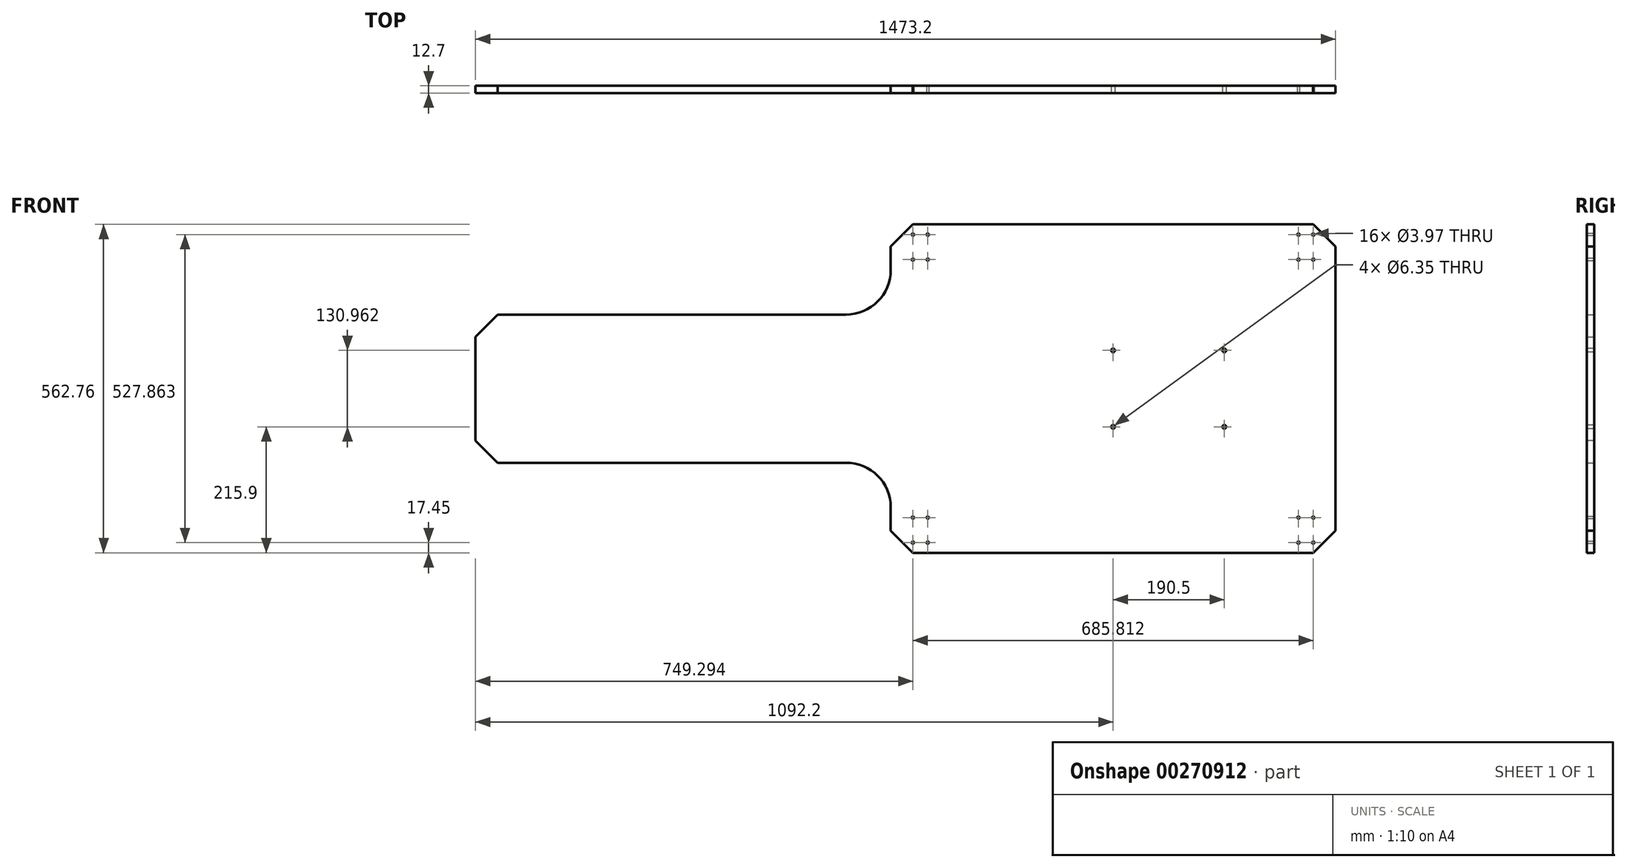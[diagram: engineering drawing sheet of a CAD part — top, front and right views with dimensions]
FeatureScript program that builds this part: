
annotation { "Feature Type Name" : "Feature", "Feature Type Description" : "" }
export const myFeature = defineFeature(function(context is Context, id is Id, definition is map)
    precondition{}
    {
        {
            var Q0;
            Q0=qCreatedBy(makeId("Front.planeOp"),FACE);
            var sketch = newSketch(context, id + "F0", { "sketchPlane" : qUnion([Q0])});
            skLineSegment(sketch, "E0", {"start": v(711.2, 0) * mm, "end": v(1473.2, 0) * mm});
            skLineSegment(sketch, "E1.0", {"start": v(711.2, 562.76) * mm, "end": v(1473.2, 562.76) * mm});
            skLineSegment(sketch, "E2", {"start": v(1473.2, 562.76) * mm, "end": v(1473.2, 0) * mm});
            skLineSegment(sketch, "E3.0", {"start": v(711.2, 0) * mm, "end": v(711.2, 78.18) * mm});
            skLineSegment(sketch, "E4.0", {"start": v(635, 408.38) * mm, "end": v(0, 408.38) * mm});
            skLineSegment(sketch, "E5.MirrorCS", {"start": v(635, 154.38) * mm, "end": v(0, 154.38) * mm});
            skLineSegment(sketch, "E6.trimOffspring", {"start": v(711.2, 484.58) * mm, "end": v(711.2, 562.76) * mm});
            skArc(sketch, "E7.filletArc", {"start": v(635, 408.38) * mm, "mid": v(688.88, 430.7) * mm, "end": v(711.2, 484.58) * mm});
            skArc(sketch, "E8.filletArc", {"start": v(711.2, 78.18) * mm, "mid": v(688.88, 132.06) * mm, "end": v(635, 154.38) * mm});
            skLineSegment(sketch, "E9", {"start": v(0, 408.38) * mm, "end": v(0, 154.38) * mm});
            skSolve(sketch);
        }
        {
            var Q0;
            Q0 = qSketchRegion(id + "F0", true);
            extrude(context, id + "F1", {"entities" : qUnion([Q0]), "depth" : 12.7 * mm});
        }
        {
            var Q0;
            Q0=makeQuery(id+"F1.opExtrude","SWEPT_EDGE",EDGE,{"disambiguationData":[OSD([sQuery(id+"F0.wireOp",EDGE,"E1.0"),sQuery(id+"F0.wireOp",EDGE,"E6.trimOffspring")])]});
            var Q1;
            Q1=makeQuery(id+"F1.opExtrude","SWEPT_EDGE",EDGE,{"disambiguationData":[OSD([sQuery(id+"F0.wireOp",EDGE,"E0"),sQuery(id+"F0.wireOp",EDGE,"E3.0")])]});
            var Q2;
            Q2=makeQuery(id+"F1.opExtrude","SWEPT_EDGE",EDGE,{"disambiguationData":[OSD([sQuery(id+"F0.wireOp",EDGE,"E0"),sQuery(id+"F0.wireOp",EDGE,"E2")])]});
            var Q3;
            Q3=makeQuery(id+"F1.opExtrude","SWEPT_EDGE",EDGE,{"disambiguationData":[OSD([sQuery(id+"F0.wireOp",EDGE,"E1.0"),sQuery(id+"F0.wireOp",EDGE,"E2")])]});
            var Q4;
            Q4=makeQuery(id+"F1.opExtrude","SWEPT_EDGE",EDGE,{"disambiguationData":[OSD([sQuery(id+"F0.wireOp",EDGE,"E5.MirrorCS"),sQuery(id+"F0.wireOp",EDGE,"E9")])]});
            var Q5;
            Q5=makeQuery(id+"F1.opExtrude","SWEPT_EDGE",EDGE,{"disambiguationData":[OSD([sQuery(id+"F0.wireOp",EDGE,"E4.0"),sQuery(id+"F0.wireOp",EDGE,"E9")])]});
            chamfer(context, id + "F2", {"entities" : qUnion([Q0, Q1, Q2, Q3, Q4, Q5]), "chamferType" : ChamferType.OFFSET_ANGLE, "width" : 38.1 * mm, "oppositeDirection" : false, "angle" : 45 * degree, "tangentPropagation" : true});
        }
        {
            var Q0;
            Q0=makeQuery(id+"F1.opExtrude","CAP_FACE",FACE,{"disambiguationData":[OSD([sQuery(id+"F0.wireOp",EDGE,"E0"),sQuery(id+"F0.wireOp",EDGE,"E1.0"),sQuery(id+"F0.wireOp",EDGE,"E2"),sQuery(id+"F0.wireOp",EDGE,"E3.0"),sQuery(id+"F0.wireOp",EDGE,"E4.0"),sQuery(id+"F0.wireOp",EDGE,"E5.MirrorCS"),sQuery(id+"F0.wireOp",EDGE,"E6.trimOffspring"),sQuery(id+"F0.wireOp",EDGE,"E7.filletArc"),sQuery(id+"F0.wireOp",EDGE,"E8.filletArc"),sQuery(id+"F0.wireOp",EDGE,"E9")])],"isStart":false});
            var sketch = newSketch(context, id + "F3", { "sketchPlane" : qUnion([Q0])});
            skCircle(sketch, "E10", {"center": v(1282.7, 346.86) * mm, "radius": 3.18 * mm});
            skCircle(sketch, "E11", {"center": v(1282.7, 215.9) * mm, "radius": 3.18 * mm});
            skPoint(sketch, "E12.endSnap0", {"position": v(1092.2, 215.9) * mm});
            skCircle(sketch, "E13", {"center": v(1092.2, 346.86) * mm, "radius": 3.18 * mm});
            skCircle(sketch, "E14", {"center": v(1092.2, 215.9) * mm, "radius": 3.18 * mm});
            skLineSegment(sketch, "E15", {"start": v(1282.7, 346.86) * mm, "end": v(500.57, 346.86) * mm});
            skLineSegment(sketch, "E16", {"start": v(1282.7, 215.9) * mm, "end": v(476.65, 215.9) * mm});
            skSolve(sketch);
        }
        {
            var Q0;
            Q0=sQuery(id+"F3.wireOp",VERTEX,"E12.endSnap0");
            var Q1;
            Q1=sQuery(id+"F3.wireOp",VERTEX,"E13.center");
            var Q2;
            Q2=sQuery(id+"F3.wireOp",VERTEX,"E10.center");
            var Q3;
            Q3=sQuery(id+"F3.wireOp",VERTEX,"E11.center");
            var Q4;
            Q4=makeQuery(id+"F1.opExtrude","SWEPT_BODY",BODY,{"disambiguationData":[OSD([sQuery(id+"F0.wireOp",EDGE,"E0"),sQuery(id+"F0.wireOp",EDGE,"E1.0"),sQuery(id+"F0.wireOp",EDGE,"E2"),sQuery(id+"F0.wireOp",EDGE,"E3.0"),sQuery(id+"F0.wireOp",EDGE,"E4.0"),sQuery(id+"F0.wireOp",EDGE,"E5.MirrorCS"),sQuery(id+"F0.wireOp",EDGE,"E6.trimOffspring"),sQuery(id+"F0.wireOp",EDGE,"E7.filletArc"),sQuery(id+"F0.wireOp",EDGE,"E8.filletArc"),sQuery(id+"F0.wireOp",EDGE,"E9")])]});
            hole(context, id + "F4", {"style" : HoleStyle.SIMPLE, "endStyle" : HoleEndStyle.THROUGH, "holeDiameter" : 6.35 * mm, "tappedDepth" : 12.7 * mm, "tapClearance" : 3, "locations" : qUnion([Q0, Q1, Q2, Q3]), "scope" : qUnion([Q4])});
        }
        {
            var Q0;
            Q0=makeQuery(id+"F1.opExtrude","CAP_FACE",FACE,{"disambiguationData":[OSD([sQuery(id+"F0.wireOp",EDGE,"E0"),sQuery(id+"F0.wireOp",EDGE,"E1.0"),sQuery(id+"F0.wireOp",EDGE,"E2"),sQuery(id+"F0.wireOp",EDGE,"E3.0"),sQuery(id+"F0.wireOp",EDGE,"E4.0"),sQuery(id+"F0.wireOp",EDGE,"E5.MirrorCS"),sQuery(id+"F0.wireOp",EDGE,"E6.trimOffspring"),sQuery(id+"F0.wireOp",EDGE,"E7.filletArc"),sQuery(id+"F0.wireOp",EDGE,"E8.filletArc"),sQuery(id+"F0.wireOp",EDGE,"E9")])],"isStart":false});
            var sketch = newSketch(context, id + "F5", { "sketchPlane" : qUnion([Q0])});
            skLineSegment(sketch, "E17", {"start": v(1422.4, 38.89) * mm, "end": v(1422.4, 0) * mm});
            skPoint(sketch, "E18", {"position": v(1422.4, 38.89) * mm});
            skLineSegment(sketch, "E19", {"start": v(1422.4, 38.89) * mm, "end": v(1422.4, 60.32) * mm});
            skLineSegment(sketch, "E20", {"start": v(1422.4, 60.32) * mm, "end": v(1435.1, 60.32) * mm});
            skLineSegment(sketch, "E21.MirrorCS", {"start": v(1422.4, 60.32) * mm, "end": v(1409.7, 60.32) * mm});
            skPoint(sketch, "E22", {"position": v(1409.7, 60.32) * mm});
            skPoint(sketch, "E23", {"position": v(1435.1, 60.32) * mm});
            skLineSegment(sketch, "E24", {"start": v(1422.4, 38.89) * mm, "end": v(1395.35, 38.89) * mm});
            skLineSegment(sketch, "E25.MirrorCS", {"start": v(1422.4, 17.45) * mm, "end": v(1409.7, 17.45) * mm});
            skLineSegment(sketch, "E26.MirrorCS", {"start": v(1422.4, 17.45) * mm, "end": v(1435.1, 17.45) * mm});
            skPoint(sketch, "E27", {"position": v(1409.7, 17.45) * mm});
            skPoint(sketch, "E28", {"position": v(1435.1, 17.45) * mm});
            skLineSegment(sketch, "E29.MirrorCS", {"start": v(762, 60.32) * mm, "end": v(774.7, 60.32) * mm});
            skLineSegment(sketch, "E30.MirrorCS", {"start": v(762, 38.89) * mm, "end": v(762, 60.32) * mm});
            skLineSegment(sketch, "E31.MirrorCS", {"start": v(762, 17.45) * mm, "end": v(774.7, 17.45) * mm});
            skLineSegment(sketch, "E32.MirrorCS", {"start": v(762, 60.32) * mm, "end": v(749.3, 60.32) * mm});
            skLineSegment(sketch, "E33.MirrorCS", {"start": v(762, 17.45) * mm, "end": v(749.3, 17.45) * mm});
            skLineSegment(sketch, "E34.MirrorCS", {"start": v(762, 38.89) * mm, "end": v(789.05, 38.89) * mm});
            skLineSegment(sketch, "E35.MirrorCS", {"start": v(762, 38.89) * mm, "end": v(762, 0) * mm});
            skPoint(sketch, "E36.MirrorP", {"position": v(762, 38.89) * mm});
            skPoint(sketch, "E37.MirrorP", {"position": v(749.3, 60.32) * mm});
            skPoint(sketch, "E38.MirrorP", {"position": v(749.3, 17.45) * mm});
            skPoint(sketch, "E39.MirrorP", {"position": v(774.7, 17.45) * mm});
            skPoint(sketch, "E40.MirrorP", {"position": v(774.7, 60.32) * mm});
            skLineSegment(sketch, "E41.MirrorCS", {"start": v(1422.4, 523.88) * mm, "end": v(1422.4, 502.44) * mm});
            skLineSegment(sketch, "E42.MirrorCS", {"start": v(1422.4, 502.44) * mm, "end": v(1409.7, 502.44) * mm});
            skLineSegment(sketch, "E43.MirrorCS", {"start": v(1422.4, 545.31) * mm, "end": v(1409.7, 545.31) * mm});
            skLineSegment(sketch, "E44.MirrorCS", {"start": v(1422.4, 502.44) * mm, "end": v(1435.1, 502.44) * mm});
            skLineSegment(sketch, "E45.MirrorCS", {"start": v(1422.4, 545.31) * mm, "end": v(1435.1, 545.31) * mm});
            skLineSegment(sketch, "E46.MirrorCS", {"start": v(1422.4, 523.88) * mm, "end": v(1422.4, 562.76) * mm});
            skLineSegment(sketch, "E47.MirrorCS", {"start": v(1422.4, 523.88) * mm, "end": v(1395.35, 523.88) * mm});
            skPoint(sketch, "E48.MirrorP", {"position": v(1422.4, 523.88) * mm});
            skPoint(sketch, "E49.MirrorP", {"position": v(1435.1, 502.44) * mm});
            skPoint(sketch, "E50.MirrorP", {"position": v(1409.7, 545.31) * mm});
            skPoint(sketch, "E51.MirrorP", {"position": v(1435.1, 545.31) * mm});
            skPoint(sketch, "E52.MirrorP", {"position": v(1409.7, 502.44) * mm});
            skLineSegment(sketch, "E53.MirrorCS", {"start": v(762, 545.31) * mm, "end": v(774.7, 545.31) * mm});
            skLineSegment(sketch, "E54.MirrorCS", {"start": v(762, 523.88) * mm, "end": v(762, 502.44) * mm});
            skLineSegment(sketch, "E55.MirrorCS", {"start": v(762, 502.44) * mm, "end": v(774.7, 502.44) * mm});
            skLineSegment(sketch, "E56.MirrorCS", {"start": v(762, 502.44) * mm, "end": v(749.3, 502.44) * mm});
            skLineSegment(sketch, "E57.MirrorCS", {"start": v(762, 545.31) * mm, "end": v(749.3, 545.31) * mm});
            skLineSegment(sketch, "E58.MirrorCS", {"start": v(762, 523.88) * mm, "end": v(789.05, 523.88) * mm});
            skLineSegment(sketch, "E59.MirrorCS", {"start": v(762, 523.88) * mm, "end": v(762, 562.76) * mm});
            skPoint(sketch, "E60.MirrorP", {"position": v(774.7, 545.31) * mm});
            skPoint(sketch, "E61.MirrorP", {"position": v(749.3, 545.31) * mm});
            skPoint(sketch, "E62.MirrorP", {"position": v(762, 523.88) * mm});
            skPoint(sketch, "E63.MirrorP", {"position": v(749.3, 502.44) * mm});
            skPoint(sketch, "E64.MirrorP", {"position": v(774.7, 502.44) * mm});
            skSolve(sketch);
        }
        {
            var Q0;
            Q0=sQuery(id+"F5.wireOp",VERTEX,"E61.MirrorP");
            var Q1;
            Q1=sQuery(id+"F5.wireOp",VERTEX,"E63.MirrorP");
            var Q2;
            Q2=sQuery(id+"F5.wireOp",VERTEX,"E64.MirrorP");
            var Q3;
            Q3=sQuery(id+"F5.wireOp",VERTEX,"E60.MirrorP");
            var Q4;
            Q4=sQuery(id+"F5.wireOp",VERTEX,"E37.MirrorP");
            var Q5;
            Q5=sQuery(id+"F5.wireOp",VERTEX,"E39.MirrorP");
            var Q6;
            Q6=sQuery(id+"F5.wireOp",VERTEX,"E38.MirrorP");
            var Q7;
            Q7=sQuery(id+"F5.wireOp",VERTEX,"E40.MirrorP");
            var Q8;
            Q8=sQuery(id+"F5.wireOp",VERTEX,"E52.MirrorP");
            var Q9;
            Q9=sQuery(id+"F5.wireOp",VERTEX,"E49.MirrorP");
            var Q10;
            Q10=sQuery(id+"F5.wireOp",VERTEX,"E51.MirrorP");
            var Q11;
            Q11=sQuery(id+"F5.wireOp",VERTEX,"E50.MirrorP");
            var Q12;
            Q12=sQuery(id+"F5.wireOp",VERTEX,"E27");
            var Q13;
            Q13=sQuery(id+"F5.wireOp",VERTEX,"E28");
            var Q14;
            Q14=sQuery(id+"F5.wireOp",VERTEX,"E23");
            var Q15;
            Q15=sQuery(id+"F5.wireOp",VERTEX,"E22");
            var Q16;
            Q16=makeQuery(id+"F1.opExtrude","SWEPT_BODY",BODY,{"disambiguationData":[OSD([sQuery(id+"F0.wireOp",EDGE,"E0"),sQuery(id+"F0.wireOp",EDGE,"E1.0"),sQuery(id+"F0.wireOp",EDGE,"E2"),sQuery(id+"F0.wireOp",EDGE,"E3.0"),sQuery(id+"F0.wireOp",EDGE,"E4.0"),sQuery(id+"F0.wireOp",EDGE,"E5.MirrorCS"),sQuery(id+"F0.wireOp",EDGE,"E6.trimOffspring"),sQuery(id+"F0.wireOp",EDGE,"E7.filletArc"),sQuery(id+"F0.wireOp",EDGE,"E8.filletArc"),sQuery(id+"F0.wireOp",EDGE,"E9")])]});
            hole(context, id + "F6", {"style" : HoleStyle.SIMPLE, "endStyle" : HoleEndStyle.THROUGH, "holeDiameter" : 3.97 * mm, "tappedDepth" : 12.7 * mm, "tapClearance" : 3, "locations" : qUnion([Q0, Q1, Q2, Q3, Q4, Q5, Q6, Q7, Q8, Q9, Q10, Q11, Q12, Q13, Q14, Q15]), "scope" : qUnion([Q16])});
        }
    });
